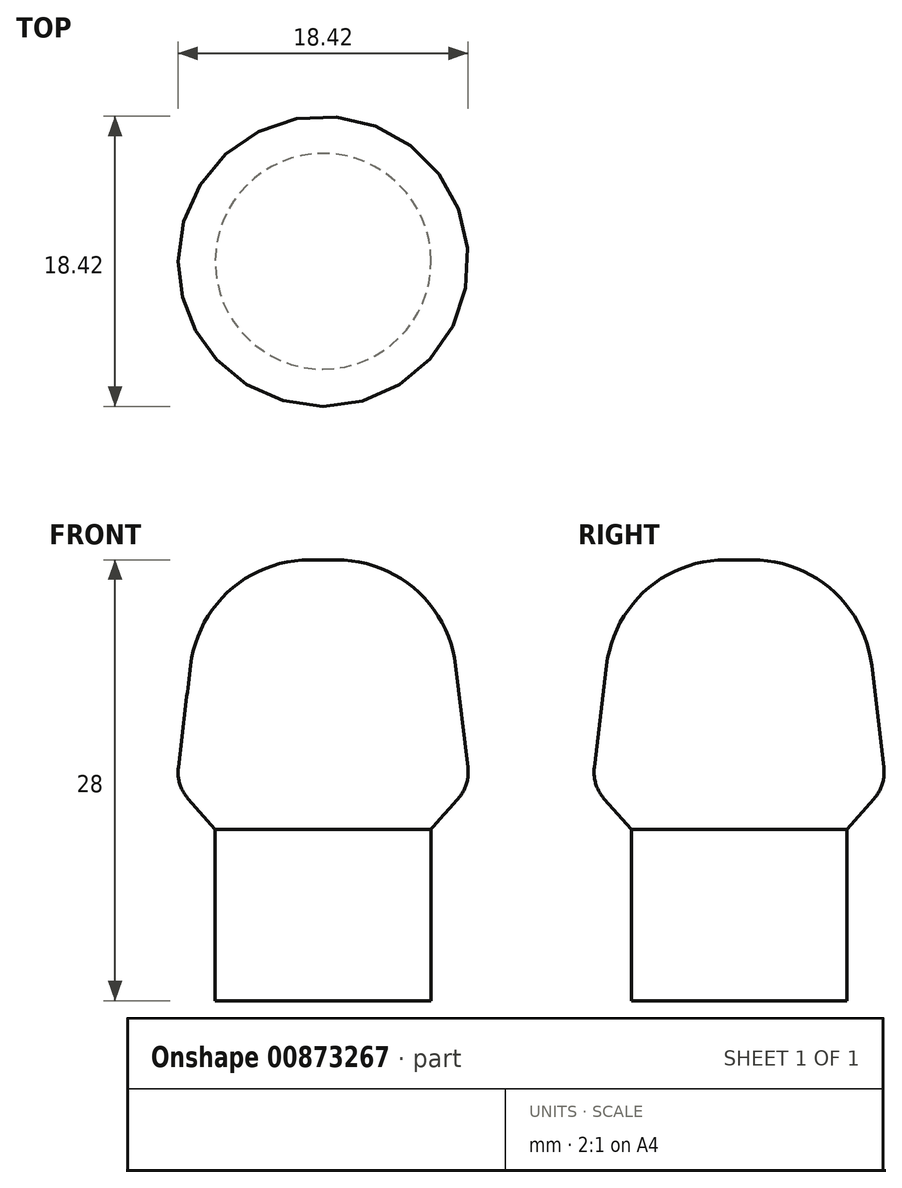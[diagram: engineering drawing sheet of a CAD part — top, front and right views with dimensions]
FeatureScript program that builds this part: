
annotation { "Feature Type Name" : "Feature", "Feature Type Description" : "" }
export const myFeature = defineFeature(function(context is Context, id is Id, definition is map)
    precondition{}
    {
        {
            var Q0;
            Q0=qCreatedBy(makeId("Top.planeOp"),FACE);
            var sketch = newSketch(context, id + "F0", { "sketchPlane" : qUnion([Q0])});
            skCircle(sketch, "E0", {"center": v(0, 0) * mm, "radius": 6.85 * mm});
            skCircle(sketch, "E1", {"center": v(0, 0) * mm, "radius": 10.18 * mm});
            skSolve(sketch);
        }
        {
            var Q0;
            Q0=makeQuery(id+"F0.imprint","IMPRINT",FACE,{"disambiguationData":[TD([[makeQuery(id+"F0.imprint","IMPRINT",EDGE,{"derivedFrom":sQuery(id+"F0.wireOp",EDGE,"E0")}),1.0]])]});
            extrude(context, id + "F1", {"entities" : qUnion([Q0]), "depth" : -8 * mm, "offsetDistance" : 25.4 * mm});
        }
        {
            var Q0;
            Q0=qCreatedBy(makeId("Front.planeOp"),FACE);
            var sketch = newSketch(context, id + "F2", { "sketchPlane" : qUnion([Q0])});
            skLineSegment(sketch, "E2", {"start": v(0, 0) * mm, "end": v(-10, 0) * mm});
            skLineSegment(sketch, "E3", {"start": v(0, 0) * mm, "end": v(0, 20) * mm});
            skLineSegment(sketch, "E4", {"start": v(0, 20) * mm, "end": v(-7.62, 20) * mm});
            skLineSegment(sketch, "E5", {"start": v(-7.62, 20) * mm, "end": v(-10, 0) * mm});
            skSolve(sketch);
        }
        {
            var Q0;
            Q0 = qSketchRegion(id + "F2", true);
            var Q1;
            Q1=sQuery(id+"F2.wireOp",EDGE,"E3");
            revolve(context, id + "F3", {"operationType" : NewBodyOperationType.ADD, "surfaceOperationType" : NewSurfaceOperationType.NEW, "entities" : qUnion([Q0]), "axis" : qUnion([Q1]), "revolveType" : RevolveType.FULL});
        }
        {
            var Q0;
            Q0=makeQuery(id+"F3.opRevolve","SWEPT_EDGE",EDGE,{"disambiguationData":[OSD([sQuery(id+"F2.wireOp",EDGE,"E4"),sQuery(id+"F2.wireOp",EDGE,"E5")])]});
            fillet(context, id + "F4", {"entities" : qUnion([Q0]), "radius" : 7.62 * mm, "tangentPropagation" : true, "allowEdgeOverflow" : false});
        }
        {
            var Q0;
            Q0=makeQuery(id+"F3.opRevolve","SWEPT_EDGE",EDGE,{"disambiguationData":[OSD([sQuery(id+"F2.wireOp",EDGE,"E2"),sQuery(id+"F2.wireOp",EDGE,"E5")])]});
            chamfer(context, id + "F5", {"entities" : qUnion([Q0]), "width" : 5.08 * mm, "tangentPropagation" : true});
        }
        {
            var Q0;
            {var subQ0=sQuery(id+"F2.wireOp",EDGE,"E5");Q0=makeQuery(id+"F5.opChamfer","BLEND_EDGE",EDGE,{"blendedFrom":[makeQuery(id+"F3.opRevolve","SWEPT_EDGE",EDGE,{"disambiguationData":[OSD([sQuery(id+"F2.wireOp",EDGE,"E2"),subQ0])]}),makeQuery(id+"F3.opRevolve","SWEPT_FACE",FACE,{"disambiguationData":[OSD([subQ0])]})],"blendedInto":[makeQuery(id+"F3.opRevolve","SWEPT_FACE",FACE,{"disambiguationData":[OSD([subQ0])]})]});}
            fillet(context, id + "F6", {"entities" : qUnion([Q0]), "radius" : 2.54 * mm, "tangentPropagation" : true, "allowEdgeOverflow" : false});
        }
    });
